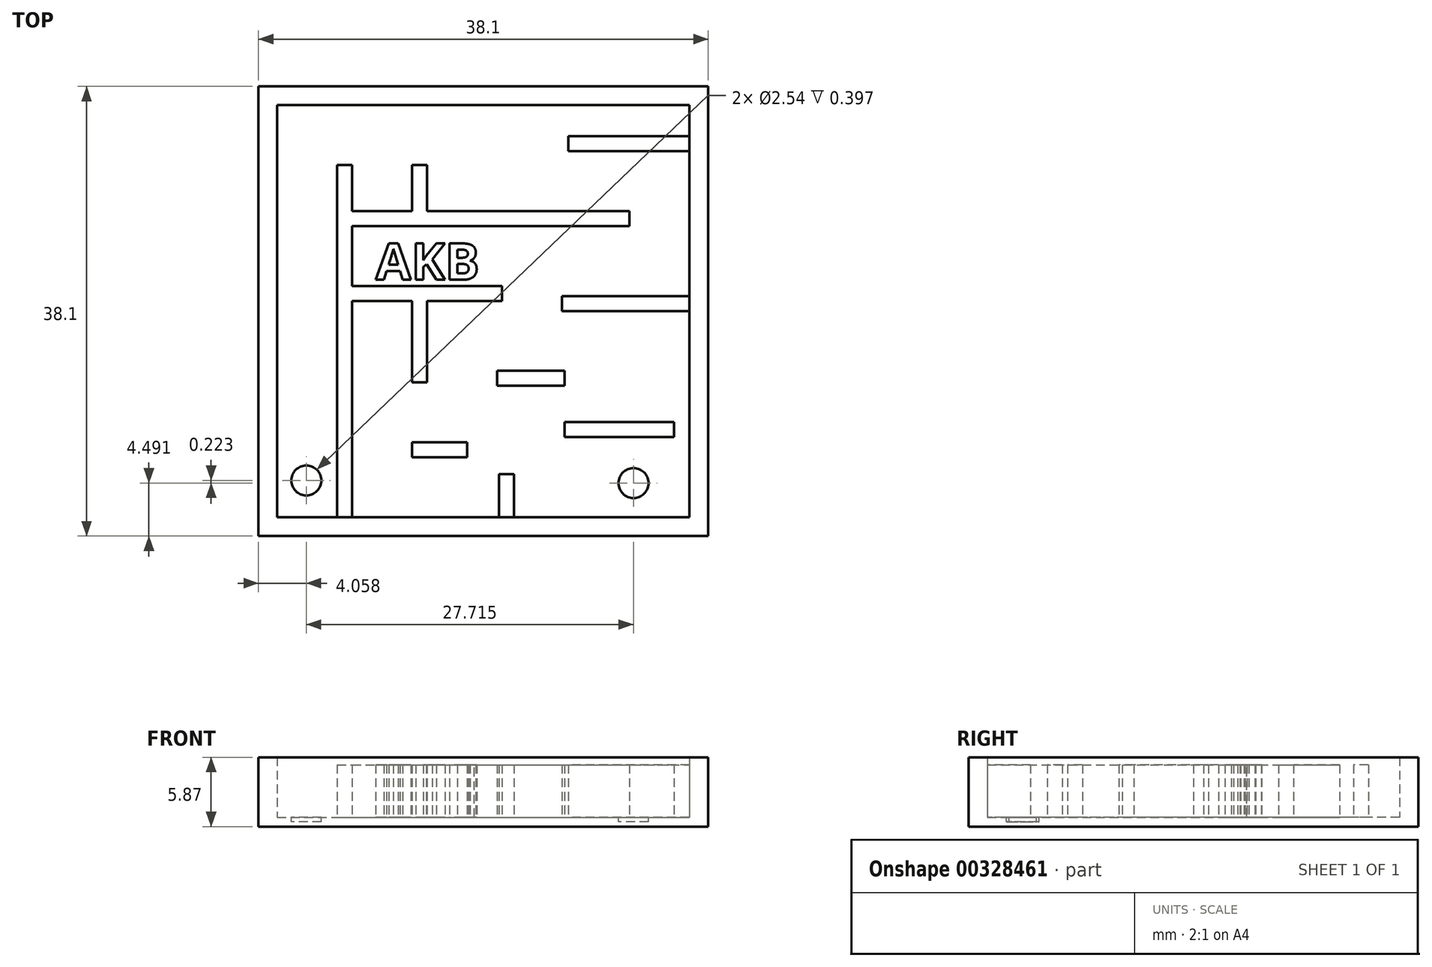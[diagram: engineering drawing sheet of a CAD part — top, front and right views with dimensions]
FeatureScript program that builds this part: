
annotation { "Feature Type Name" : "Feature", "Feature Type Description" : "" }
export const myFeature = defineFeature(function(context is Context, id is Id, definition is map)
    precondition{}
    {
        {
            var Q0;
            Q0=qCreatedBy(makeId("Top.planeOp"),FACE);
            var sketch = newSketch(context, id + "F0", { "sketchPlane" : qUnion([Q0])});
            skLineSegment(sketch, "E0.bottom", {"start": v(-21.58, 22.38) * mm, "end": v(16.52, 22.38) * mm});
            skLineSegment(sketch, "E0.top", {"start": v(-21.58, -15.72) * mm, "end": v(16.52, -15.72) * mm});
            skLineSegment(sketch, "E0.left", {"start": v(-21.58, 22.38) * mm, "end": v(-21.58, -15.72) * mm});
            skLineSegment(sketch, "E0.right", {"start": v(16.52, 22.38) * mm, "end": v(16.52, -15.72) * mm});
            skSolve(sketch);
        }
        {
            var Q0;
            Q0=makeQuery(id+"F0.imprint","IMPRINT",FACE,{"disambiguationData":[TD([[makeQuery(id+"F0.imprint","IMPRINT",EDGE,{"derivedFrom":sQuery(id+"F0.wireOp",EDGE,"E0.bottom")}),-1.0]])]});
            extrude(context, id + "F1", {"entities" : qUnion([Q0]), "depth" : 0.8 * mm});
        }
        {
            var Q0;
            Q0=makeQuery(id+"F1.opExtrude","CAP_FACE",FACE,{"disambiguationData":[OSD([sQuery(id+"F0.wireOp",EDGE,"E0.bottom"),sQuery(id+"F0.wireOp",EDGE,"E0.top"),sQuery(id+"F0.wireOp",EDGE,"E0.left"),sQuery(id+"F0.wireOp",EDGE,"E0.right")])],"isStart":false});
            var sketch = newSketch(context, id + "F2", { "sketchPlane" : qUnion([Q0])});
            skLineSegment(sketch, "E1.0", {"start": v(-20, 20.8) * mm, "end": v(14.93, 20.8) * mm});
            skLineSegment(sketch, "E1.1", {"start": v(-20, 20.8) * mm, "end": v(-20, -14.13) * mm});
            skLineSegment(sketch, "E1.2", {"start": v(-20, -14.13) * mm, "end": v(14.93, -14.13) * mm});
            skLineSegment(sketch, "E1.3", {"start": v(14.93, 20.8) * mm, "end": v(14.93, -14.13) * mm});
            skSolve(sketch);
        }
        {
            var Q0;
            Q0=makeQuery(id+"F2.imprint","IMPRINT",FACE,{"disambiguationData":[TD([[makeQuery(id+"F2.imprint","IMPRINT",EDGE,{"derivedFrom":sQuery(id+"F2.wireOp",EDGE,"E1.0")}),1.0]])]});
            extrude(context, id + "F3", {"entities" : qUnion([Q0]), "operationType" : NewBodyOperationType.ADD, "depth" : 5.08 * mm});
        }
        {
            var Q0;
            Q0=makeQuery(id+"F1.opExtrude","CAP_FACE",FACE,{"disambiguationData":[OSD([sQuery(id+"F0.wireOp",EDGE,"E0.bottom"),sQuery(id+"F0.wireOp",EDGE,"E0.top"),sQuery(id+"F0.wireOp",EDGE,"E0.left"),sQuery(id+"F0.wireOp",EDGE,"E0.right")])],"isStart":false});
            var sketch = newSketch(context, id + "F4", { "sketchPlane" : qUnion([Q0])});
            skLineSegment(sketch, "E2.bottom", {"start": v(-14.92, -14.13) * mm, "end": v(-13.65, -14.13) * mm});
            skLineSegment(sketch, "E2.top", {"start": v(-14.92, 15.72) * mm, "end": v(-13.65, 15.72) * mm});
            skLineSegment(sketch, "E2.left", {"start": v(-14.92, -14.13) * mm, "end": v(-14.92, 15.72) * mm});
            skLineSegment(sketch, "E2.right", {"start": v(-13.65, -14.13) * mm, "end": v(-13.65, 15.72) * mm});
            skLineSegment(sketch, "E3.bottom", {"start": v(-13.65, 10.53) * mm, "end": v(9.85, 10.53) * mm});
            skLineSegment(sketch, "E3.top", {"start": v(-13.65, 11.8) * mm, "end": v(-8.57, 11.8) * mm});
            skLineSegment(sketch, "E3.left", {"start": v(-13.65, 10.53) * mm, "end": v(-13.65, 11.8) * mm});
            skLineSegment(sketch, "E3.right", {"start": v(9.85, 10.53) * mm, "end": v(9.85, 11.8) * mm});
            skLineSegment(sketch, "E4.left", {"start": v(-8.57, 11.8) * mm, "end": v(-8.57, 15.7) * mm});
            skLineSegment(sketch, "E5.bottom", {"start": v(14.93, 18.15) * mm, "end": v(4.67, 18.15) * mm});
            skLineSegment(sketch, "E5.top", {"start": v(14.93, 16.88) * mm, "end": v(4.67, 16.88) * mm});
            skLineSegment(sketch, "E5.left", {"start": v(14.93, 18.15) * mm, "end": v(14.93, 16.88) * mm});
            skLineSegment(sketch, "E5.right", {"start": v(4.67, 18.15) * mm, "end": v(4.67, 16.88) * mm});
            skLineSegment(sketch, "E6.bottom", {"start": v(4.13, 4.6) * mm, "end": v(14.93, 4.6) * mm});
            skLineSegment(sketch, "E6.top", {"start": v(4.13, 3.33) * mm, "end": v(14.93, 3.33) * mm});
            skLineSegment(sketch, "E6.left", {"start": v(4.13, 4.6) * mm, "end": v(4.13, 3.33) * mm});
            skLineSegment(sketch, "E6.right", {"start": v(14.93, 4.6) * mm, "end": v(14.93, 3.33) * mm});
            skLineSegment(sketch, "E7.bottom", {"start": v(-13.65, 5.45) * mm, "end": v(-0.95, 5.45) * mm});
            skLineSegment(sketch, "E7.top", {"start": v(-13.65, 4.18) * mm, "end": v(-8.57, 4.18) * mm});
            skLineSegment(sketch, "E7.left", {"start": v(-13.65, 5.45) * mm, "end": v(-13.65, 4.18) * mm});
            skLineSegment(sketch, "E7.right", {"start": v(-0.95, 5.45) * mm, "end": v(-0.95, 4.18) * mm});
            skLineSegment(sketch, "E8.bottom", {"start": v(-1.37, -1.72) * mm, "end": v(4.37, -1.72) * mm});
            skLineSegment(sketch, "E8.top", {"start": v(-1.37, -3) * mm, "end": v(4.37, -3) * mm});
            skLineSegment(sketch, "E8.left", {"start": v(-1.37, -1.72) * mm, "end": v(-1.37, -3) * mm});
            skLineSegment(sketch, "E8.right", {"start": v(4.37, -1.72) * mm, "end": v(4.37, -3) * mm});
            skLineSegment(sketch, "E9.bottom", {"start": v(4.37, -6.06) * mm, "end": v(13.63, -6.06) * mm});
            skLineSegment(sketch, "E9.top", {"start": v(4.37, -7.33) * mm, "end": v(13.63, -7.33) * mm});
            skLineSegment(sketch, "E9.left", {"start": v(4.37, -6.06) * mm, "end": v(4.37, -7.33) * mm});
            skLineSegment(sketch, "E9.right", {"start": v(13.63, -6.06) * mm, "end": v(13.63, -7.33) * mm});
            skLineSegment(sketch, "E10.bottom", {"start": v(-8.57, -7.78) * mm, "end": v(-3.91, -7.78) * mm});
            skLineSegment(sketch, "E10.top", {"start": v(-8.57, -9.05) * mm, "end": v(-3.91, -9.05) * mm});
            skLineSegment(sketch, "E10.left", {"start": v(-8.57, -7.78) * mm, "end": v(-8.57, -9.05) * mm});
            skLineSegment(sketch, "E10.right", {"start": v(-3.91, -7.78) * mm, "end": v(-3.91, -9.05) * mm});
            skLineSegment(sketch, "E11.bottom", {"start": v(-1.2, -10.46) * mm, "end": v(0.06, -10.46) * mm});
            skLineSegment(sketch, "E11.top", {"start": v(-1.2, -14.13) * mm, "end": v(0.06, -14.13) * mm});
            skLineSegment(sketch, "E11.left", {"start": v(-1.2, -10.46) * mm, "end": v(-1.2, -14.13) * mm});
            skLineSegment(sketch, "E11.right", {"start": v(0.06, -10.46) * mm, "end": v(0.06, -14.13) * mm});
            skPoint(sketch, "E12.oppositeSnap0", {"position": v(-7.3, 4.18) * mm});
            skLineSegment(sketch, "E12.top", {"start": v(-8.57, -2.7) * mm, "end": v(-7.3, -2.7) * mm});
            skLineSegment(sketch, "E12.left", {"start": v(-8.57, 4.18) * mm, "end": v(-8.57, -2.7) * mm});
            skLineSegment(sketch, "E12.right", {"start": v(-7.3, 4.18) * mm, "end": v(-7.3, -2.7) * mm});
            skLineSegment(sketch, "E13.trimOffspring", {"start": v(-7.3, 4.18) * mm, "end": v(-0.95, 4.18) * mm});
            skLineSegment(sketch, "E14.trimOffspring", {"start": v(-7.3, 11.8) * mm, "end": v(9.85, 11.8) * mm});
            skLineSegment(sketch, "E15", {"start": v(-8.57, 15.7) * mm, "end": v(-7.3, 15.7) * mm});
            skLineSegment(sketch, "E16", {"start": v(-7.3, 15.7) * mm, "end": v(-7.3, 11.8) * mm});
            skSolve(sketch);
        }
        {
            var Q0;
            {var subQ1=sQuery(id+"F4.wireOp",EDGE,"E2.bottom");Q0=makeQuery(id+"F4.imprint","IMPRINT",FACE,{"disambiguationData":[TD([[makeQuery(id+"F4.imprint","IMPRINT",EDGE,{"derivedFrom":subQ1}),1.0]])]});}
            var Q1;
            Q1=makeQuery(id+"F4.imprint","IMPRINT",FACE,{"disambiguationData":[TD([[makeQuery(id+"F4.imprint","IMPRINT",EDGE,{"derivedFrom":sQuery(id+"F4.wireOp",EDGE,"E7.bottom")}),-1.0]])]});
            var Q2;
            Q2=makeQuery(id+"F4.imprint","IMPRINT",FACE,{"disambiguationData":[TD([[makeQuery(id+"F4.imprint","IMPRINT",EDGE,{"derivedFrom":sQuery(id+"F4.wireOp",EDGE,"E3.bottom")}),1.0]])]});
            var Q3;
            Q3=makeQuery(id+"F4.imprint","IMPRINT",FACE,{"disambiguationData":[TD([[makeQuery(id+"F4.imprint","IMPRINT",EDGE,{"derivedFrom":sQuery(id+"F4.wireOp",EDGE,"E8.bottom")}),-1.0]])]});
            var Q4;
            Q4=makeQuery(id+"F4.imprint","IMPRINT",FACE,{"disambiguationData":[TD([[makeQuery(id+"F4.imprint","IMPRINT",EDGE,{"derivedFrom":sQuery(id+"F4.wireOp",EDGE,"E10.bottom")}),-1.0]])]});
            var Q5;
            Q5=makeQuery(id+"F4.imprint","IMPRINT",FACE,{"disambiguationData":[TD([[makeQuery(id+"F4.imprint","IMPRINT",EDGE,{"derivedFrom":sQuery(id+"F4.wireOp",EDGE,"E11.bottom")}),-1.0]])]});
            var Q6;
            Q6=makeQuery(id+"F4.imprint","IMPRINT",FACE,{"disambiguationData":[TD([[makeQuery(id+"F4.imprint","IMPRINT",EDGE,{"derivedFrom":sQuery(id+"F4.wireOp",EDGE,"E9.bottom")}),-1.0]])]});
            var Q7;
            Q7=makeQuery(id+"F4.imprint","IMPRINT",FACE,{"disambiguationData":[TD([[makeQuery(id+"F4.imprint","IMPRINT",EDGE,{"derivedFrom":sQuery(id+"F4.wireOp",EDGE,"E6.bottom")}),-1.0]])]});
            var Q8;
            Q8=makeQuery(id+"F4.imprint","IMPRINT",FACE,{"disambiguationData":[TD([[makeQuery(id+"F4.imprint","IMPRINT",EDGE,{"derivedFrom":sQuery(id+"F4.wireOp",EDGE,"E5.bottom")}),1.0]])]});
            extrude(context, id + "F5", {"entities" : qUnion([Q0, Q1, Q2, Q3, Q4, Q5, Q6, Q7, Q8]), "operationType" : NewBodyOperationType.ADD, "depth" : 4.44 * mm});
        }
        {
            var Q0;
            {var subQ5=sQuery(id+"F4.wireOp",EDGE,"E2.top");Q0=makeQuery(id+"F4.imprint","IMPRINT",FACE,{"disambiguationData":[TD([[makeQuery(id+"F4.imprint","IMPRINT",EDGE,{"derivedFrom":subQ5}),1.0]])]});}
            var sketch = newSketch(context, id + "F6", { "sketchPlane" : qUnion([Q0])});
            skLineSegment(sketch, "E17", {"start": v(-20.05, -14.08) * mm, "end": v(-15, -14.08) * mm});
            skCircle(sketch, "E18", {"center": v(-17.52, -11) * mm, "radius": 1.27 * mm});
            skPoint(sketch, "E18.centerSnap0", {"position": v(-17.52, -14.08) * mm});
            skLineSegment(sketch, "E19", {"start": v(5.47, -14.11) * mm, "end": v(14.91, -14.11) * mm});
            skCircle(sketch, "E20", {"center": v(10.2, -11.23) * mm, "radius": 1.27 * mm});
            skPoint(sketch, "E20.centerSnap0", {"position": v(10.2, -14.11) * mm});
            skSolve(sketch);
        }
        {
            var Q0;
            Q0 = qSketchRegion(id + "F6", true);
            extrude(context, id + "F7", {"entities" : qUnion([Q0]), "operationType" : NewBodyOperationType.REMOVE, "oppositeDirection" : true, "depth" : 0.4 * mm});
        }
        {
            var Q0;
            Q0 = qSketchRegion(id + "F6", true);
            extrude(context, id + "F8", {"entities" : qUnion([Q0]), "operationType" : NewBodyOperationType.REMOVE, "oppositeDirection" : true, "depth" : 0.4 * mm});
        }
        {
            var Q0;
            {var subQ5=sQuery(id+"F4.wireOp",EDGE,"E2.top");Q0=makeQuery(id+"F4.imprint","IMPRINT",FACE,{"disambiguationData":[TD([[makeQuery(id+"F4.imprint","IMPRINT",EDGE,{"derivedFrom":subQ5}),1.0]])]});}
            var sketch = newSketch(context, id + "F9", { "sketchPlane" : qUnion([Q0])});
            skText(sketch, "E21", { "text": "AKB", "fontName": "OpenSans-Bold.ttf"});
            const initialGuessF9  = {"E21": [-0.01164, 0.00599, 1, 0, 0.00312]};
            skSetInitialGuess(sketch, initialGuessF9);
            skSolve(sketch);
        }
        {
            var Q0;
            Q0 = qSketchRegion(id + "F9", true);
            extrude(context, id + "F10", {"entities" : qUnion([Q0]), "operationType" : NewBodyOperationType.ADD, "depth" : 4.44 * mm});
        }
    });
